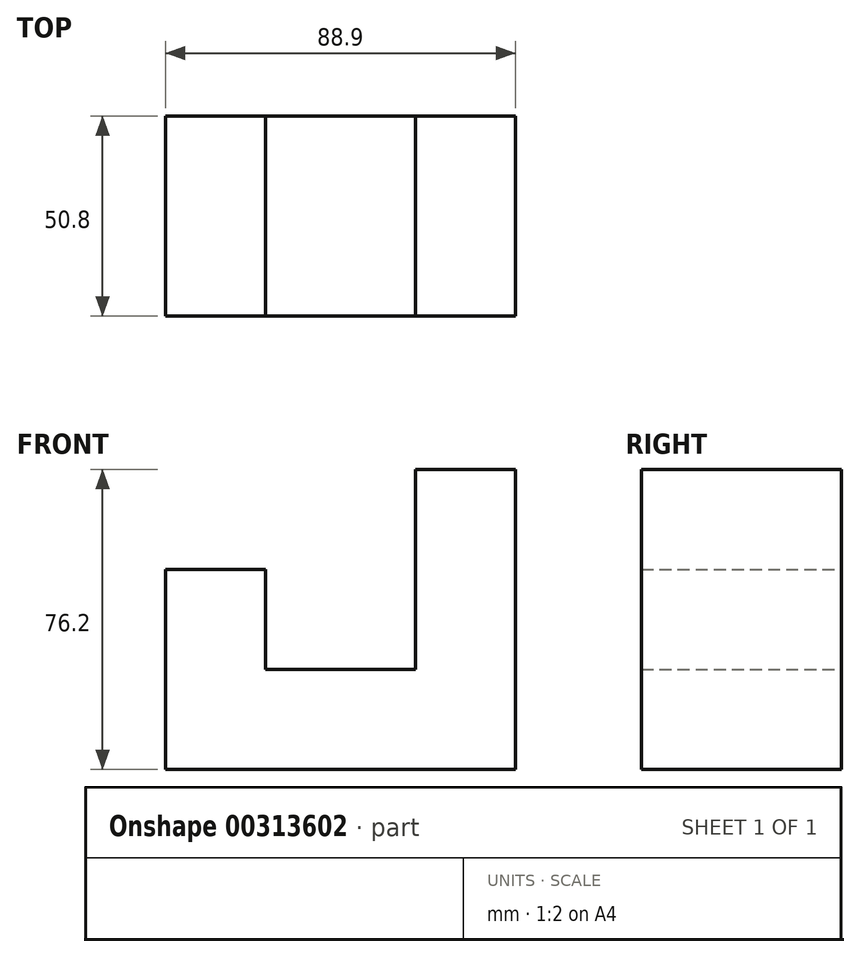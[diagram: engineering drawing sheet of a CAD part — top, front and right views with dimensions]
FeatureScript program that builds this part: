
annotation { "Feature Type Name" : "Feature", "Feature Type Description" : "" }
export const myFeature = defineFeature(function(context is Context, id is Id, definition is map)
    precondition{}
    {
        {
            var Q0;
            Q0=qCreatedBy(makeId("Front.planeOp"),FACE);
            var sketch = newSketch(context, id + "F0", { "sketchPlane" : qUnion([Q0])});
            skLineSegment(sketch, "E0", {"start": v(-53.25, -43.57) * mm, "end": v(35.65, -43.57) * mm});
            skLineSegment(sketch, "E1", {"start": v(35.65, -43.57) * mm, "end": v(35.65, 32.63) * mm});
            skLineSegment(sketch, "E2", {"start": v(35.65, 32.63) * mm, "end": v(10.25, 32.63) * mm});
            skLineSegment(sketch, "E3", {"start": v(10.25, 32.63) * mm, "end": v(10.25, -18.17) * mm});
            skLineSegment(sketch, "E4", {"start": v(10.25, -18.17) * mm, "end": v(-27.85, -18.17) * mm});
            skLineSegment(sketch, "E5", {"start": v(-27.85, -18.17) * mm, "end": v(-27.85, 7.23) * mm});
            skLineSegment(sketch, "E6", {"start": v(-27.85, 7.23) * mm, "end": v(-53.25, 7.23) * mm});
            skLineSegment(sketch, "E7", {"start": v(-53.25, 7.23) * mm, "end": v(-53.25, -18.17) * mm});
            skLineSegment(sketch, "E8", {"start": v(-53.25, -18.17) * mm, "end": v(-53.25, -43.57) * mm});
            skSolve(sketch);
        }
        {
            var Q0;
            Q0=makeQuery(id+"F0.imprint","IMPRINT",FACE,{"disambiguationData":[TD([[makeQuery(id+"F0.imprint","IMPRINT",EDGE,{"derivedFrom":sQuery(id+"F0.wireOp",EDGE,"E0")}),1.0]])]});
            extrude(context, id + "F1", {"entities" : qUnion([Q0]), "depth" : 50.8 * mm});
        }
    });
